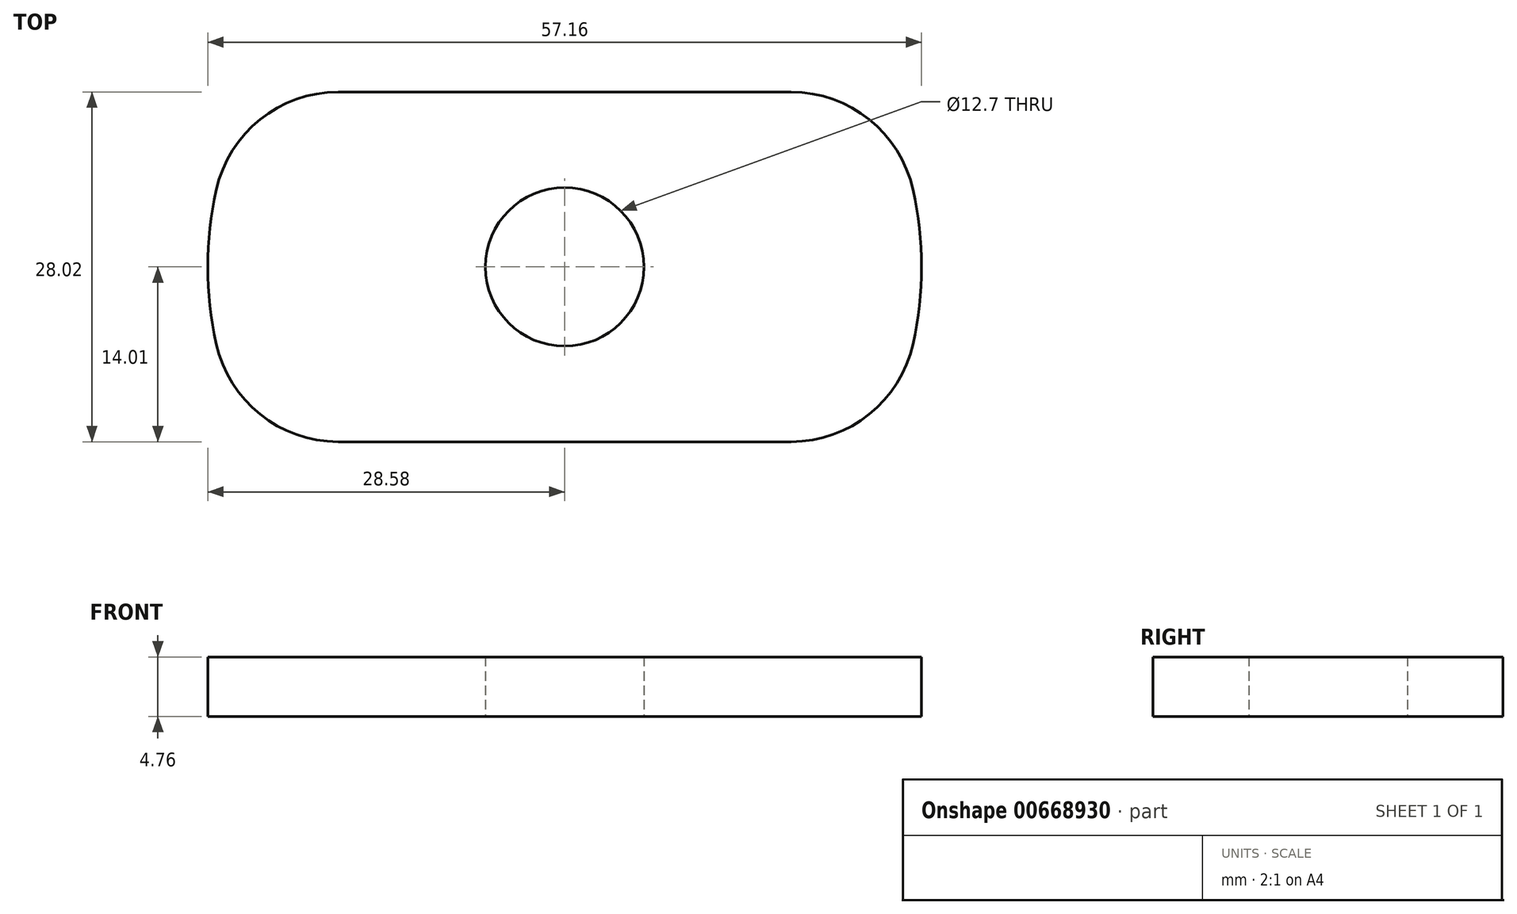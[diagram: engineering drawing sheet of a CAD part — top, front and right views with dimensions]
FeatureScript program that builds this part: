
annotation { "Feature Type Name" : "Feature", "Feature Type Description" : "" }
export const myFeature = defineFeature(function(context is Context, id is Id, definition is map)
    precondition{}
    {
        {
            var Q0;
            Q0=qCreatedBy(makeId("Top.planeOp"),FACE);
            var sketch = newSketch(context, id + "F0", { "sketchPlane" : qUnion([Q0])});
            skCircle(sketch, "E0", {"center": v(0, 0) * mm, "radius": 6.35 * mm});
            skCircle(sketch, "E1", {"center": v(0, 0) * mm, "radius": 28.58 * mm});
            skLineSegment(sketch, "E2", {"start": v(0, 0) * mm, "end": v(-28.58, 0) * mm});
            skLineSegment(sketch, "E3", {"start": v(0, 0) * mm, "end": v(28.58, 0) * mm});
            skLineSegment(sketch, "E4", {"start": v(0, 0) * mm, "end": v(0, 28.58) * mm});
            skLineSegment(sketch, "E5", {"start": v(0, 0) * mm, "end": v(0, -28.58) * mm});
            skLineSegment(sketch, "E6", {"start": v(0, -6.35) * mm, "end": v(27.86, -6.35) * mm});
            skLineSegment(sketch, "E7", {"start": v(0, 6.35) * mm, "end": v(27.86, 6.35) * mm});
            skLineSegment(sketch, "E8", {"start": v(0, -6.35) * mm, "end": v(-27.86, -6.35) * mm});
            skLineSegment(sketch, "E9", {"start": v(0, 6.35) * mm, "end": v(-27.86, 6.35) * mm});
            skCircle(sketch, "E10", {"center": v(0, 0) * mm, "radius": 14.01 * mm});
            skLineSegment(sketch, "E11", {"start": v(0, 14.01) * mm, "end": v(24.9, 14.01) * mm});
            skPoint(sketch, "E11.startSnap0", {"position": v(0, 14.29) * mm});
            skLineSegment(sketch, "E12", {"start": v(0, -14.01) * mm, "end": v(24.9, -14.01) * mm});
            skLineSegment(sketch, "E13", {"start": v(0, -14.01) * mm, "end": v(-24.9, -14.01) * mm});
            skLineSegment(sketch, "E14", {"start": v(0, 14.01) * mm, "end": v(-24.9, 14.01) * mm});
            skSolve(sketch);
        }
        {
            var Q0;
            {var subQ1=sQuery(id+"F0.wireOp",EDGE,"E0");var subQ3=sQuery(id+"F0.wireOp",EDGE,"E2");var subQ4=makeQuery(id+"F0.imprint","INTERSECT",VERTEX,{"derivedFrom":[subQ1,subQ3]});Q0=makeQuery(id+"F0.imprint","IMPRINT",FACE,{"disambiguationData":[TD([[makeQuery(id+"F0.imprint","IMPRINT",EDGE,{"disambiguationData":[TD([[subQ4,-1.0]])],"derivedFrom":subQ3}),-1.0]])]});}
            var Q1;
            {var subQ1=sQuery(id+"F0.wireOp",EDGE,"E0");var subQ3=sQuery(id+"F0.wireOp",EDGE,"E3");var subQ4=makeQuery(id+"F0.imprint","INTERSECT",VERTEX,{"derivedFrom":[subQ1,subQ3]});Q1=makeQuery(id+"F0.imprint","IMPRINT",FACE,{"disambiguationData":[TD([[makeQuery(id+"F0.imprint","IMPRINT",EDGE,{"disambiguationData":[TD([[subQ4,-1.0]])],"derivedFrom":subQ3}),1.0]])]});}
            var Q2;
            {var subQ0=sQuery(id+"F0.wireOp",EDGE,"E6");var subQ3=sQuery(id+"F0.wireOp",EDGE,"E10");var subQ5=makeQuery(id+"F0.imprint","INTERSECT",VERTEX,{"derivedFrom":[subQ0,subQ3]});Q2=makeQuery(id+"F0.imprint","IMPRINT",FACE,{"disambiguationData":[TD([[makeQuery(id+"F0.imprint","IMPRINT",EDGE,{"disambiguationData":[TD([[subQ5,1.0]])],"derivedFrom":subQ0}),-1.0]])]});}
            var Q3;
            {var subQ0=sQuery(id+"F0.wireOp",EDGE,"E8");var subQ3=sQuery(id+"F0.wireOp",EDGE,"E10");var subQ5=makeQuery(id+"F0.imprint","INTERSECT",VERTEX,{"derivedFrom":[subQ0,subQ3]});Q3=makeQuery(id+"F0.imprint","IMPRINT",FACE,{"disambiguationData":[TD([[makeQuery(id+"F0.imprint","IMPRINT",EDGE,{"disambiguationData":[TD([[subQ5,1.0]])],"derivedFrom":subQ0}),1.0]])]});}
            var Q4;
            {var subQ1=sQuery(id+"F0.wireOp",EDGE,"E0");var subQ3=sQuery(id+"F0.wireOp",EDGE,"E2");var subQ4=makeQuery(id+"F0.imprint","INTERSECT",VERTEX,{"derivedFrom":[subQ1,subQ3]});Q4=makeQuery(id+"F0.imprint","IMPRINT",FACE,{"disambiguationData":[TD([[makeQuery(id+"F0.imprint","IMPRINT",EDGE,{"disambiguationData":[TD([[subQ4,-1.0]])],"derivedFrom":subQ3}),1.0]])]});}
            var Q5;
            {var subQ0=sQuery(id+"F0.wireOp",EDGE,"E2");var subQ1=sQuery(id+"F0.wireOp",EDGE,"E1");var subQ2=makeQuery(id+"F0.imprint","INTERSECT",VERTEX,{"derivedFrom":[subQ1,subQ0]});Q5=makeQuery(id+"F0.imprint","IMPRINT",FACE,{"disambiguationData":[TD([[makeQuery(id+"F0.imprint","IMPRINT",EDGE,{"disambiguationData":[TD([[subQ2,-1.0]])],"derivedFrom":subQ1}),1.0]])]});}
            var Q6;
            {var subQ0=sQuery(id+"F0.wireOp",EDGE,"E3");var subQ1=sQuery(id+"F0.wireOp",EDGE,"E1");var subQ2=makeQuery(id+"F0.imprint","INTERSECT",VERTEX,{"derivedFrom":[subQ1,subQ0]});Q6=makeQuery(id+"F0.imprint","IMPRINT",FACE,{"disambiguationData":[TD([[makeQuery(id+"F0.imprint","IMPRINT",EDGE,{"disambiguationData":[TD([[subQ2,-1.0]])],"derivedFrom":subQ1}),1.0]])]});}
            var Q7;
            {var subQ0=sQuery(id+"F0.wireOp",EDGE,"E7");var subQ3=sQuery(id+"F0.wireOp",EDGE,"E10");var subQ5=makeQuery(id+"F0.imprint","INTERSECT",VERTEX,{"derivedFrom":[subQ0,subQ3]});Q7=makeQuery(id+"F0.imprint","IMPRINT",FACE,{"disambiguationData":[TD([[makeQuery(id+"F0.imprint","IMPRINT",EDGE,{"disambiguationData":[TD([[subQ5,-1.0]])],"derivedFrom":subQ3}),1.0]])]});}
            var Q8;
            {var subQ0=sQuery(id+"F0.wireOp",EDGE,"E9");var subQ3=sQuery(id+"F0.wireOp",EDGE,"E10");var subQ5=makeQuery(id+"F0.imprint","INTERSECT",VERTEX,{"derivedFrom":[subQ0,subQ3]});Q8=makeQuery(id+"F0.imprint","IMPRINT",FACE,{"disambiguationData":[TD([[makeQuery(id+"F0.imprint","IMPRINT",EDGE,{"disambiguationData":[TD([[subQ5,1.0]])],"derivedFrom":subQ3}),1.0]])]});}
            var Q9;
            {var subQ3=sQuery(id+"F0.wireOp",EDGE,"E13");Q9=makeQuery(id+"F0.imprint","IMPRINT",FACE,{"disambiguationData":[TD([[makeQuery(id+"F0.imprint","IMPRINT",EDGE,{"derivedFrom":subQ3}),-1.0]])]});}
            var Q10;
            {var subQ3=sQuery(id+"F0.wireOp",EDGE,"E11");Q10=makeQuery(id+"F0.imprint","IMPRINT",FACE,{"disambiguationData":[TD([[makeQuery(id+"F0.imprint","IMPRINT",EDGE,{"derivedFrom":subQ3}),-1.0]])]});}
            var Q11;
            {var subQ7=sQuery(id+"F0.wireOp",EDGE,"2pYTaxKB-rvCy-OBoL-YzJV-S2jiRoCwVsng");Q11=makeQuery(id+"F0.imprint","IMPRINT",FACE,{"disambiguationData":[TD([[makeQuery(id+"F0.imprint","IMPRINT",EDGE,{"derivedFrom":subQ7}),1.0]])]});}
            var Q12;
            {var subQ1=sQuery(id+"F0.wireOp",EDGE,"E0");var subQ3=sQuery(id+"F0.wireOp",EDGE,"E3");var subQ4=makeQuery(id+"F0.imprint","INTERSECT",VERTEX,{"derivedFrom":[subQ1,subQ3]});Q12=makeQuery(id+"F0.imprint","IMPRINT",FACE,{"disambiguationData":[TD([[makeQuery(id+"F0.imprint","IMPRINT",EDGE,{"disambiguationData":[TD([[subQ4,-1.0]])],"derivedFrom":subQ3}),-1.0]])]});}
            var Q13;
            {var subQ0=sQuery(id+"F0.wireOp",EDGE,"E2");var subQ1=sQuery(id+"F0.wireOp",EDGE,"E1");var subQ2=makeQuery(id+"F0.imprint","INTERSECT",VERTEX,{"derivedFrom":[subQ1,subQ0]});Q13=makeQuery(id+"F0.imprint","IMPRINT",FACE,{"disambiguationData":[TD([[makeQuery(id+"F0.imprint","IMPRINT",EDGE,{"disambiguationData":[TD([[subQ2,1.0]])],"derivedFrom":subQ1}),1.0]])]});}
            var Q14;
            {var subQ3=sQuery(id+"F0.wireOp",EDGE,"E14");Q14=makeQuery(id+"F0.imprint","IMPRINT",FACE,{"disambiguationData":[TD([[makeQuery(id+"F0.imprint","IMPRINT",EDGE,{"derivedFrom":subQ3}),1.0]])]});}
            var Q15;
            {var subQ0=sQuery(id+"F0.wireOp",EDGE,"E3");var subQ1=sQuery(id+"F0.wireOp",EDGE,"E1");var subQ2=makeQuery(id+"F0.imprint","INTERSECT",VERTEX,{"derivedFrom":[subQ1,subQ0]});Q15=makeQuery(id+"F0.imprint","IMPRINT",FACE,{"disambiguationData":[TD([[makeQuery(id+"F0.imprint","IMPRINT",EDGE,{"disambiguationData":[TD([[subQ2,1.0]])],"derivedFrom":subQ1}),1.0]])]});}
            var Q16;
            {var subQ3=sQuery(id+"F0.wireOp",EDGE,"E12");Q16=makeQuery(id+"F0.imprint","IMPRINT",FACE,{"disambiguationData":[TD([[makeQuery(id+"F0.imprint","IMPRINT",EDGE,{"derivedFrom":subQ3}),1.0]])]});}
            extrude(context, id + "F1", {"entities" : qUnion([Q0, Q1, Q2, Q3, Q4, Q5, Q6, Q7, Q8, Q9, Q10, Q11, Q12, Q13, Q14, Q15, Q16]), "depth" : 4.76 * mm, "offsetDistance" : 25.4 * mm});
        }
        {
            var Q0;
            Q0=makeQuery(id+"F1.opExtrude","SWEPT_EDGE",EDGE,{"disambiguationData":[OSD([sQuery(id+"F0.wireOp",EDGE,"E1"),sQuery(id+"F0.wireOp",EDGE,"E11")])]});
            var Q1;
            Q1=makeQuery(id+"F1.opExtrude","SWEPT_EDGE",EDGE,{"disambiguationData":[OSD([sQuery(id+"F0.wireOp",EDGE,"E1"),sQuery(id+"F0.wireOp",EDGE,"E14")])]});
            var Q2;
            Q2=makeQuery(id+"F1.opExtrude","SWEPT_EDGE",EDGE,{"disambiguationData":[OSD([sQuery(id+"F0.wireOp",EDGE,"E1"),sQuery(id+"F0.wireOp",EDGE,"E12")])]});
            var Q3;
            Q3=makeQuery(id+"F1.opExtrude","SWEPT_EDGE",EDGE,{"disambiguationData":[OSD([sQuery(id+"F0.wireOp",EDGE,"E1"),sQuery(id+"F0.wireOp",EDGE,"E13")])]});
            fillet(context, id + "F2", {"entities" : qUnion([Q0, Q1, Q2, Q3]), "radius" : 10 * mm, "tangentPropagation" : true, "allowEdgeOverflow" : false});
        }
    });
